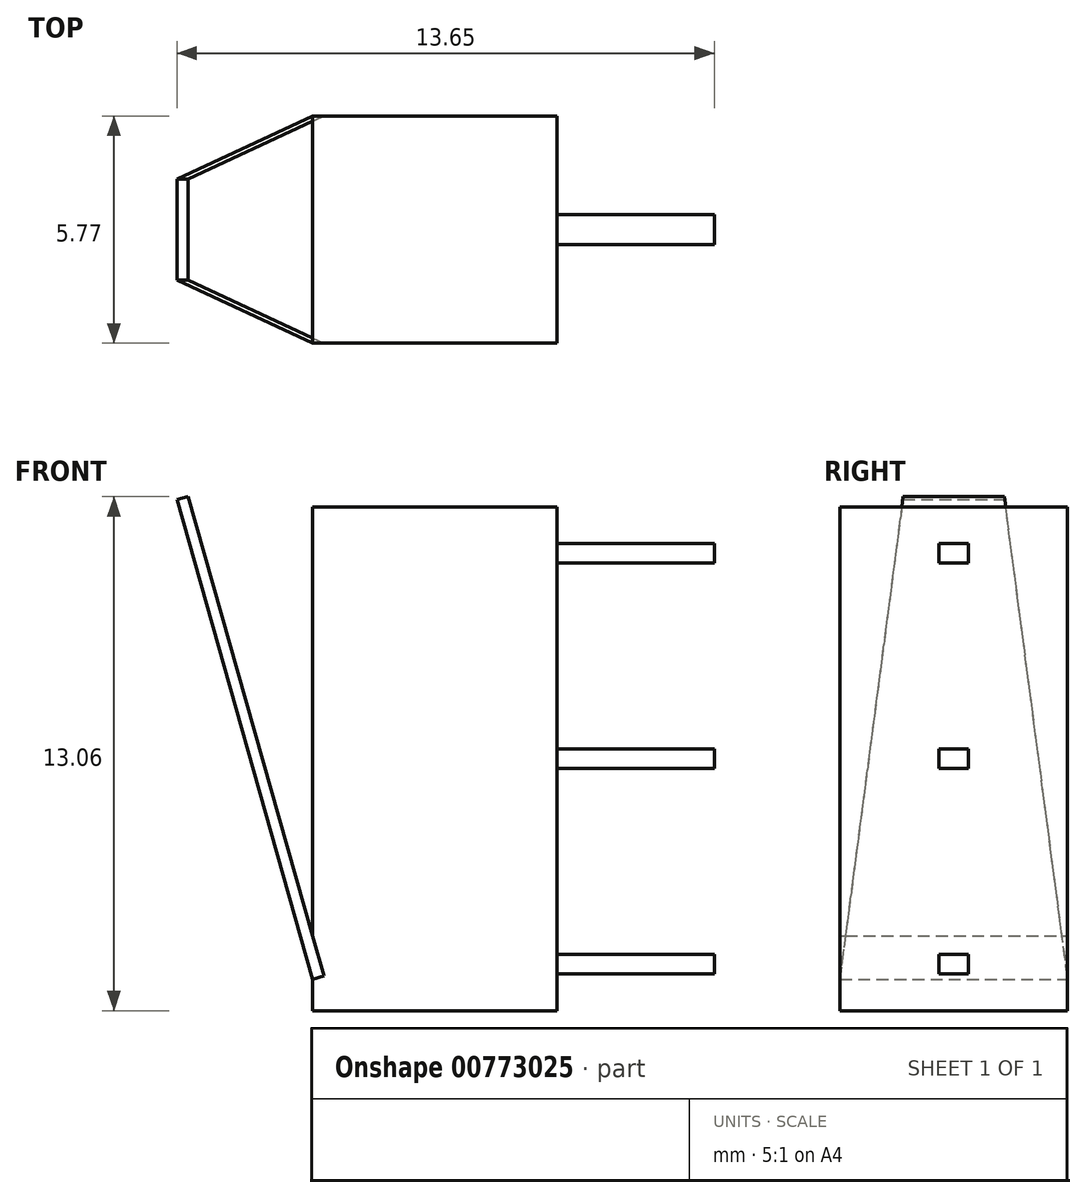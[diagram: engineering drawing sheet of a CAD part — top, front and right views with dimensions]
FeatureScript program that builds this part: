
annotation { "Feature Type Name" : "Feature", "Feature Type Description" : "" }
export const myFeature = defineFeature(function(context is Context, id is Id, definition is map)
    precondition{}
    {
        {
            var Q0;
            Q0=qCreatedBy(makeId("Front.planeOp"),FACE);
            var sketch = newSketch(context, id + "F0", { "sketchPlane" : qUnion([Q0])});
            skLineSegment(sketch, "E0.bottom", {"start": v(3.1, 6.4) * mm, "end": v(-3.1, 6.4) * mm});
            skLineSegment(sketch, "E0.top", {"start": v(3.1, -6.4) * mm, "end": v(-3.1, -6.4) * mm});
            skLineSegment(sketch, "E0.left", {"start": v(3.1, 6.4) * mm, "end": v(3.1, -6.4) * mm});
            skLineSegment(sketch, "E0.right", {"start": v(-3.1, 6.4) * mm, "end": v(-3.1, -6.4) * mm});
            skPoint(sketch, "E0.middle", {"position": v(0, 0) * mm});
            skSolve(sketch);
        }
        {
            var Q0;
            Q0 = qSketchRegion(id + "F0", true);
            extrude(context, id + "F1", {"entities" : qUnion([Q0]), "depth" : 5.77 * mm, "offsetDistance" : 25.4 * mm});
        }
        {
            var Q0;
            Q0=makeQuery(id+"F1.opExtrude","SWEPT_FACE",FACE,{"disambiguationData":[OSD([sQuery(id+"F0.wireOp",EDGE,"E0.left")])]});
            var sketch = newSketch(context, id + "F2", { "sketchPlane" : qUnion([Q0])});
            skLineSegment(sketch, "E1", {"start": v(-2.88, 0) * mm, "end": v(-2.89, 5.47) * mm, "construction": true});
            skLineSegment(sketch, "E2", {"start": v(-5.77, 0) * mm, "end": v(0, 0) * mm, "construction": true});
            skLineSegment(sketch, "E3.bottom", {"start": v(-2.89, 5.47) * mm, "end": v(-2.5, 5.47) * mm});
            skLineSegment(sketch, "E3.top", {"start": v(-2.88, 4.97) * mm, "end": v(-2.5, 4.97) * mm});
            skLineSegment(sketch, "E3.left", {"start": v(-2.89, 5.47) * mm, "end": v(-2.89, 4.97) * mm});
            skLineSegment(sketch, "E3.right", {"start": v(-2.5, 5.47) * mm, "end": v(-2.5, 4.97) * mm});
            skLineSegment(sketch, "E4.bottom", {"start": v(-2.51, 0.25) * mm, "end": v(-3.26, 0.25) * mm});
            skLineSegment(sketch, "E4.top", {"start": v(-2.51, -0.25) * mm, "end": v(-3.26, -0.25) * mm});
            skLineSegment(sketch, "E4.left", {"start": v(-2.51, 0.25) * mm, "end": v(-2.51, -0.25) * mm});
            skLineSegment(sketch, "E4.right", {"start": v(-3.26, 0.25) * mm, "end": v(-3.26, -0.25) * mm});
            skPoint(sketch, "E4.middle", {"position": v(-2.88, 0) * mm});
            skLineSegment(sketch, "E5.MirrorCS", {"start": v(-3.26, 5.47) * mm, "end": v(-3.26, 4.97) * mm});
            skLineSegment(sketch, "E6.MirrorCS", {"start": v(-2.89, 4.97) * mm, "end": v(-3.26, 4.97) * mm});
            skLineSegment(sketch, "E7.MirrorCS", {"start": v(-2.89, 5.47) * mm, "end": v(-3.26, 5.47) * mm});
            skLineSegment(sketch, "E8.MirrorCS", {"start": v(-2.51, 0.25) * mm, "end": v(-2.5, -0.25) * mm});
            skLineSegment(sketch, "E9.MirrorCS", {"start": v(-3.26, 0.25) * mm, "end": v(-2.51, 0.25) * mm});
            skLineSegment(sketch, "E10.MirrorCS", {"start": v(-3.26, -0.25) * mm, "end": v(-2.51, -0.25) * mm});
            skLineSegment(sketch, "E11.MirrorCS", {"start": v(0, 0) * mm, "end": v(-5.77, 0) * mm, "construction": true});
            skLineSegment(sketch, "E12.MirrorCS", {"start": v(-2.89, -5.47) * mm, "end": v(-2.89, -4.97) * mm});
            skLineSegment(sketch, "E13.MirrorCS", {"start": v(-2.51, -0.25) * mm, "end": v(-2.51, 0.25) * mm});
            skLineSegment(sketch, "E14.MirrorCS", {"start": v(-3.26, -0.25) * mm, "end": v(-3.26, 0.25) * mm});
            skLineSegment(sketch, "E15.MirrorCS", {"start": v(-3.26, -5.47) * mm, "end": v(-3.26, -4.97) * mm});
            skLineSegment(sketch, "E16.MirrorCS", {"start": v(-2.5, -5.47) * mm, "end": v(-2.5, -4.97) * mm});
            skLineSegment(sketch, "E17.MirrorCS", {"start": v(-2.89, -4.97) * mm, "end": v(-3.26, -4.97) * mm});
            skLineSegment(sketch, "E18.MirrorCS", {"start": v(-2.88, -4.97) * mm, "end": v(-2.5, -4.97) * mm});
            skLineSegment(sketch, "E19.MirrorCS", {"start": v(-2.89, -5.47) * mm, "end": v(-3.26, -5.47) * mm});
            skLineSegment(sketch, "E20.MirrorCS", {"start": v(-2.89, -5.47) * mm, "end": v(-2.5, -5.47) * mm});
            skLineSegment(sketch, "E21.MirrorCS", {"start": v(-2.51, -0.25) * mm, "end": v(-2.5, 0.25) * mm});
            skSolve(sketch);
        }
        {
            var Q0;
            Q0 = qSketchRegion(id + "F2", true);
            extrude(context, id + "F3", {"entities" : qUnion([Q0]), "operationType" : NewBodyOperationType.ADD, "depth" : 4 * mm, "offsetDistance" : 25 * mm});
        }
        {
            var Q0;
            Q0=makeQuery(id+"F1.opExtrude","CAP_FACE",FACE,{"disambiguationData":[OSD([sQuery(id+"F0.wireOp",EDGE,"E0.bottom"),sQuery(id+"F0.wireOp",EDGE,"E0.top"),sQuery(id+"F0.wireOp",EDGE,"E0.left"),sQuery(id+"F0.wireOp",EDGE,"E0.right")])],"isStart":false});
            var sketch = newSketch(context, id + "F4", { "sketchPlane" : qUnion([Q0])});
            skLineSegment(sketch, "E22", {"start": v(-3.1, -5.6) * mm, "end": v(-6.55, 6.58) * mm});
            skSolve(sketch);
        }
        {
            var Q0;
            Q0 = qSketchRegion(id + "F4", true);
            var Q1;
            Q1=sQuery(id+"F4.wireOp",EDGE,"E22");
            var Q2;
            Q2=makeQuery(id+"F1.opExtrude","CAP_FACE",FACE,{"disambiguationData":[OSD([sQuery(id+"F0.wireOp",EDGE,"E0.bottom"),sQuery(id+"F0.wireOp",EDGE,"E0.top"),sQuery(id+"F0.wireOp",EDGE,"E0.left"),sQuery(id+"F0.wireOp",EDGE,"E0.right")])],"isStart":true});
            extrude(context, id + "F5", {"entities" : qUnion([Q0]), "bodyType" : ToolBodyType.SURFACE, "surfaceEntities" : qUnion([Q1]), "endBound" : BoundingType.UP_TO_SURFACE, "oppositeDirection" : true, "depth" : 25 * mm, "endBoundEntityFace" : qUnion([Q2]), "offsetDistance" : 25 * mm});
        }
        {
            var Q0;
            Q0=makeQuery(id+"F5.opExtrude","SWEPT_FACE",FACE,{"disambiguationData":[OSD([sQuery(id+"F4.wireOp",EDGE,"E22")])]});
            var sketch = newSketch(context, id + "F6", { "sketchPlane" : qUnion([Q0])});
            skLineSegment(sketch, "E23.bottom", {"start": v(0, 8.12) * mm, "end": v(5.77, 8.12) * mm});
            skLineSegment(sketch, "E23.top", {"start": v(0, -4.54) * mm, "end": v(5.77, -4.54) * mm});
            skLineSegment(sketch, "E23.left", {"start": v(0, 8.12) * mm, "end": v(0, -4.54) * mm});
            skLineSegment(sketch, "E23.right", {"start": v(5.77, 8.12) * mm, "end": v(5.77, -4.54) * mm});
            skSolve(sketch);
        }
        {
            var Q0;
            Q0 = qSketchRegion(id + "F6", true);
            extrude(context, id + "F7", {"entities" : qUnion([Q0]), "operationType" : NewBodyOperationType.ADD, "oppositeDirection" : true, "depth" : .3 * mm, "offsetDistance" : 25 * mm});
        }
        {
            var Q0;
            Q0=makeQuery(id+"F7.opExtrude","CAP_FACE",FACE,{"disambiguationData":[OSD([sQuery(id+"F6.wireOp",EDGE,"E23.bottom"),sQuery(id+"F6.wireOp",EDGE,"E23.top"),sQuery(id+"F6.wireOp",EDGE,"E23.left"),sQuery(id+"F6.wireOp",EDGE,"E23.right")])],"isStart":true});
            var sketch = newSketch(context, id + "F8", { "sketchPlane" : qUnion([Q0])});
            skLineSegment(sketch, "E24", {"start": v(5.77, -4.54) * mm, "end": v(4.17, 8.12) * mm});
            skLineSegment(sketch, "E25", {"start": v(4.17, 8.12) * mm, "end": v(1.6, 8.12) * mm});
            skLineSegment(sketch, "E26", {"start": v(1.6, 8.12) * mm, "end": v(0, -4.54) * mm});
            skLineSegment(sketch, "E27", {"start": v(1.6, 8.12) * mm, "end": v(0, 8.12) * mm});
            skLineSegment(sketch, "E28", {"start": v(0, 8.12) * mm, "end": v(0, -4.54) * mm});
            skLineSegment(sketch, "E29", {"start": v(5.77, -4.54) * mm, "end": v(5.77, 8.12) * mm});
            skLineSegment(sketch, "E30", {"start": v(5.77, 8.12) * mm, "end": v(4.17, 8.12) * mm});
            skSolve(sketch);
        }
        {
            var Q0;
            Q0 = qSketchRegion(id + "F8", true);
            var Q1;
            Q1=makeQuery(id+"F7.opExtrude","CAP_FACE",FACE,{"disambiguationData":[OSD([sQuery(id+"F6.wireOp",EDGE,"E23.bottom"),sQuery(id+"F6.wireOp",EDGE,"E23.top"),sQuery(id+"F6.wireOp",EDGE,"E23.left"),sQuery(id+"F6.wireOp",EDGE,"E23.right")])],"isStart":false});
            extrude(context, id + "F9", {"entities" : qUnion([Q0]), "operationType" : NewBodyOperationType.REMOVE, "endBound" : BoundingType.UP_TO_SURFACE, "oppositeDirection" : true, "depth" : .3 * mm, "endBoundEntityFace" : qUnion([Q1]), "offsetDistance" : 25 * mm});
        }
    });
